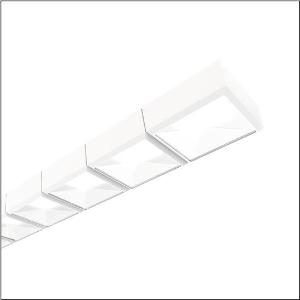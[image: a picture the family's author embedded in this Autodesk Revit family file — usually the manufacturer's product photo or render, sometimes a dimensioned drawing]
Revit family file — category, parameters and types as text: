
# Revit family: scriptus_r__11_5mz312d0twb_510a
name_source: partatom
category: Lighting Fixtures
units: mm (PartAtom-declared; Revit-internal decimal feet)

## family parameters
Cut with Voids When Loaded = No
Host = Face
Light Source = No
Part Type = Normal
Room Calculation Point = No
Round Connector Dimension = Use Diameter
Shared = No

## types (1)
- --- (1 x LED 3000K+6500K / CRI = 80 (unbekannt), 3200 lm / 2380 lm, 3000K)
    Apparent Load = 94 VA
    CIE Flux Codes = 0 0 0 0 100 / 82 95 99 100 100
    Color Rendering = 80
    Color Temperature = 3000K
    Default Elevation = 1800 mm
    Description = Scriptus® 11, office luminaire, primary optical cover: lenses, CAT 2 (L<= 3000cd/m²), light emission: direct/indirect distribution, primary light characteristic: symmetric, installation type: suspended mounting, LED, rated luminous flux: 11.150lm, luminous efficacy: 116lm/W, light colour: 8tw, colour temperature: 3000..6500K, control gear: ECG DALI, with terminal, 5-pole, mains connection: 230V, AC, 50Hz, rated input power: 96W, LED, control gear: ECG DALI, housing, luminaire housing, of aluminium, traffic white (RAL 9016), length: 1.768mm, width: 114mm, height: 57mm, protection rating (complete): IP20, insulation class (complete): insulation class I (protective earthing), certification: CE, protection symbol: F, permissible operating ambient temperature: <= +25°C, standard: EN 50419, packaging unit: 1 piece
    Height = 57 mm
    Lamp = 1 x LED 3000K+6500K / CRI >= 80 (unbekannt)
    Lamp Light Flux = 3200 lm / 2380 lm
    Lamp count = 1
    Length = 1768 mm
    Luminous efficacy = 119 lm/W
    Manufacturer = Siteco
    ModVariant = No
    Model = 5MZ312D0TWB
    Mounting Place = Ceiling
    Mounting Type = Pendant
    Number of Poles = 1
    OnlyDefault = Yes
    Power Factor = 1
    Product Name = Scriptus® 11
    Product group = office luminaire | ceiling pendant
    ProductGroupID = 902
    Protection Class = Protection class I
    Protection Degree = IP 20
    RLX_Detail_Level = 1
    RLX_Emergency_Light_Flux = 0 lm
    RLX_Emergency_Type = 0
    RLX_Emergency_Type_DB = No
    RlxData = <blob elided: 31693 chars, md5=32c4f3a6>
    Socket = socket
    Standby Power = 0 W
    System Light Flux = 11160 lm
    System Power = 94 W
    Type Comments = individual setting: colour temperature 6500K
    Type Image = l_1004839.jpg
    URL = http://relux.com
    VarID = @adj_164664
    Voltage = 0 V
    Weight = 0.00 kg
    Width = 114 mm

## geometry (parser evidence)
native form markers: Blend x4, Sweep x18
no freeform markers — native parametric forms only
